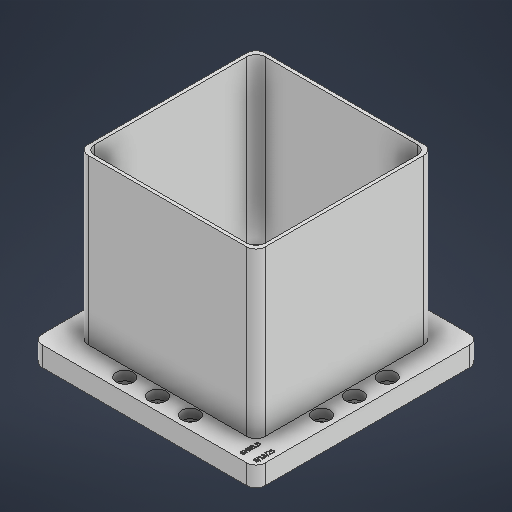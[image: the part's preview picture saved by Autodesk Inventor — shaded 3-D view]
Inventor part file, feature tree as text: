
AUTODESK INVENTOR PART (.ipt)
format: ipt  version: 2025 (Build 290162000, 162)  size: 535,552 bytes
history: native  units: in
note: dims shown in document units (in); Inventor stores cm internally (conversion verified against a paired STEP export)
features: sketch x4, extrude x3, hole x1, fillet x1
ambient origin geometry x8: Origin, YZ Plane, XZ Plane, XY Plane, X Axis, Y Axis, Z Axis, Center Point
bodies: Solid1 (feature_tree)
feature tree (9):
  extrude  "Extrusion1"  Depth=5.9055in
  hole  "Hole1"  [1 undecoded]
  extrude  "Extrusion3"  Depth=0.2362in
  fillet  "Fillet2"  Radius=0.2362in
  extrude  "Extrusion4"  Depth=0.2362in
  sketch  "Sketch1"  dims[d17=0.5906in d18=0.0in d30=5.9055in]
  sketch  "Sketch3"  dims[d31=5.9055in d32=0.2362in]
  sketch  "Sketch4"  dims[d33=0.2362in d34=0.2362in d35=0.2362in]
  sketch  "Sketch5"  dims[d36=0.2362in d37=0.2362in d38=0.9843in d39=0.9843in d40=0.9843in d41=0.9843in d42=0.2805in d43=0.2362in d44=0.5118in d45=0.2756in d46=0.0172in d47=0.315in d48=0.8108in d50=1.7717in d51=6.6929in d52=6.6929in d53=0.7874in d54=5.1181in d55=5.1181in d56=1.7717in d57=5.1181in d58=5.1181in d59=0.0984in d60=4.9213in d61=0.0in d62=0.0787in d63=0.7874in d64=0.7087in d65=0.2805in d66=0.1181in d67=0.0in d68=0.0in d69=0.0in]
note: 1 required parameter value undecoded (feature->parameter linkage not recoverable at this tier; creation-order binding heuristic only, values carry confidence <= 0.55)
